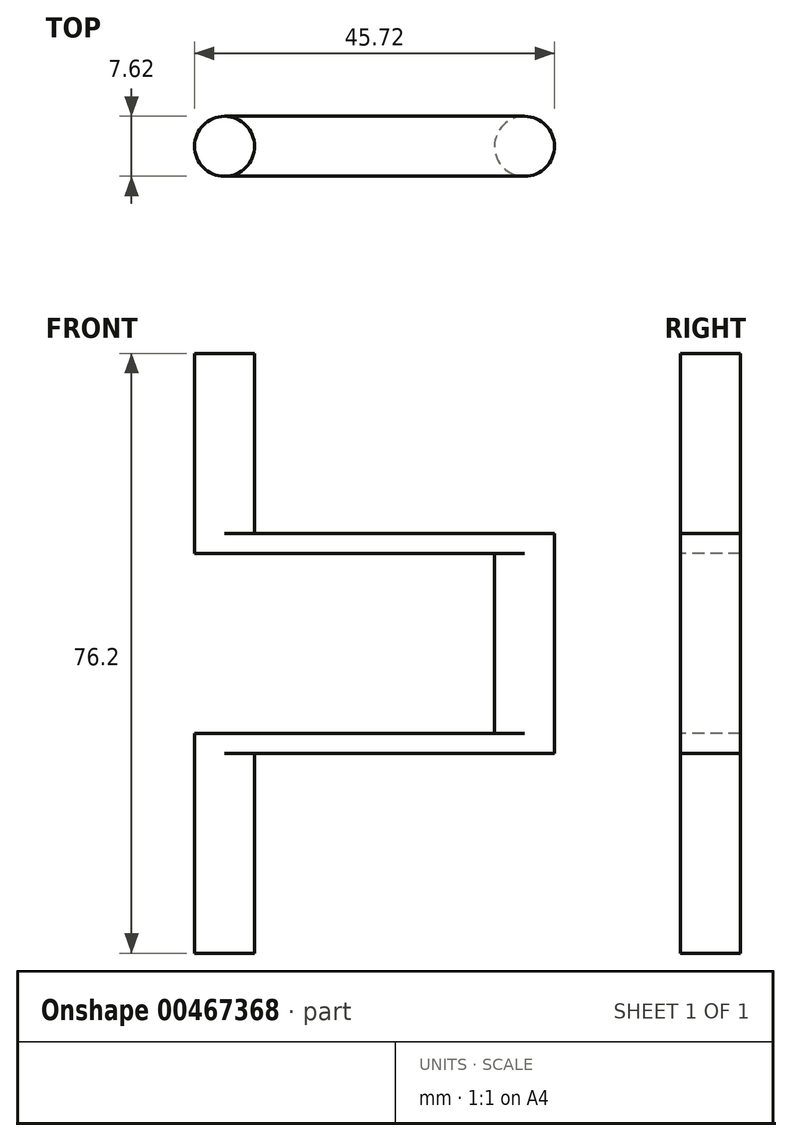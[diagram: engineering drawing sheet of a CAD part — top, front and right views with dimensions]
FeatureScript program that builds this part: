
annotation { "Feature Type Name" : "Feature", "Feature Type Description" : "" }
export const myFeature = defineFeature(function(context is Context, id is Id, definition is map)
    precondition{}
    {
        {
            var Q0;
            Q0=qCreatedBy(makeId("Top.planeOp"),FACE);
            var sketch = newSketch(context, id + "F0", { "sketchPlane" : qUnion([Q0])});
            skLineSegment(sketch, "E0.bottom", {"start": v(19.05, -3.8) * mm, "end": v(-19.05, -3.81) * mm});
            skLineSegment(sketch, "E0.top", {"start": v(19.05, 3.81) * mm, "end": v(-19.05, 3.8) * mm});
            skPoint(sketch, "E0.middle", {"position": v(0, 0) * mm});
            skCircle(sketch, "E1", {"center": v(-19.05, 0) * mm, "radius": 3.81 * mm});
            skCircle(sketch, "E2", {"center": v(19.05, 0) * mm, "radius": 3.81 * mm});
            skSolve(sketch);
        }
        {
            var Q0;
            {var subQ0=sQuery(id+"F0.wireOp",EDGE,"E0.bottom");Q0=makeQuery(id+"F0.imprint","IMPRINT",FACE,{"disambiguationData":[TD([[makeQuery(id+"F0.imprint","IMPRINT",EDGE,{"derivedFrom":subQ0}),-1.0]])]});}
            extrude(context, id + "F1", {"entities" : qUnion([Q0]), "depth" : 2.54 * mm});
        }
        {
            var Q0;
            {var subQ0=sQuery(id+"F0.wireOp",EDGE,"E2");var subQ1=makeQuery(id+"F0.imprint","INTERSECT",VERTEX,{"derivedFrom":[sQuery(id+"F0.wireOp",EDGE,"E0.bottom"),subQ0]});Q0=makeQuery(id+"F0.imprint","IMPRINT",FACE,{"disambiguationData":[TD([[makeQuery(id+"F0.imprint","IMPRINT",EDGE,{"disambiguationData":[TD([[subQ1,1.0]])],"derivedFrom":subQ0}),1.0]])]});}
            extrude(context, id + "F2", {"entities" : qUnion([Q0]), "operationType" : NewBodyOperationType.ADD, "depth" : 25.4 * mm});
        }
        {
            var Q0;
            {var subQ0=sQuery(id+"F0.wireOp",EDGE,"E1");var subQ1=makeQuery(id+"F0.imprint","INTERSECT",VERTEX,{"derivedFrom":[sQuery(id+"F0.wireOp",EDGE,"E0.bottom"),subQ0]});Q0=makeQuery(id+"F0.imprint","IMPRINT",FACE,{"disambiguationData":[TD([[makeQuery(id+"F0.imprint","IMPRINT",EDGE,{"disambiguationData":[TD([[subQ1,1.0]])],"derivedFrom":subQ0}),1.0]])]});}
            extrude(context, id + "F3", {"entities" : qUnion([Q0]), "oppositeDirection" : true, "depth" : 12.7 * mm});
        }
        {
            var Q0;
            {var subQ0=sQuery(id+"F0.wireOp",EDGE,"E1");var subQ1=makeQuery(id+"F0.imprint","INTERSECT",VERTEX,{"derivedFrom":[sQuery(id+"F0.wireOp",EDGE,"E0.bottom"),subQ0]});Q0=makeQuery(id+"F0.imprint","IMPRINT",FACE,{"disambiguationData":[TD([[makeQuery(id+"F0.imprint","IMPRINT",EDGE,{"disambiguationData":[TD([[subQ1,1.0]])],"derivedFrom":subQ0}),1.0]])]});}
            extrude(context, id + "F4", {"entities" : qUnion([Q0]), "depth" : 2.54 * mm});
        }
        {
            var Q0;
            Q0=makeQuery(id+"F2.opExtrude","CAP_FACE",FACE,{"disambiguationData":[OSD([sQuery(id+"F0.wireOp",EDGE,"E2")])],"isStart":false});
            var sketch = newSketch(context, id + "F5", { "sketchPlane" : qUnion([Q0])});
            skLineSegment(sketch, "E3.bottom", {"start": v(19.05, -3.8) * mm, "end": v(-19.05, -3.8) * mm});
            skLineSegment(sketch, "E3.top", {"start": v(19.05, 3.8) * mm, "end": v(-19.05, 3.8) * mm});
            skPoint(sketch, "E3.middle", {"position": v(0, 0) * mm});
            skArc(sketch, "E4", {"start": v(19.05, -3.81) * mm, "mid": v(22.86, 0) * mm, "end": v(19.05, 3.81) * mm});
            skCircle(sketch, "E5", {"center": v(-19.05, 0) * mm, "radius": 3.81 * mm});
            skSolve(sketch);
        }
        {
            var Q0;
            {var subQ0=sQuery(id+"F5.wireOp",EDGE,"E3.bottom");Q0=makeQuery(id+"F5.imprint","IMPRINT",FACE,{"disambiguationData":[TD([[makeQuery(id+"F5.imprint","IMPRINT",EDGE,{"derivedFrom":subQ0}),-1.0]])]});}
            var Q1;
            {var subQ0=sQuery(id+"F5.wireOp",EDGE,"E4");Q1=makeQuery(id+"F5.imprint","IMPRINT",FACE,{"disambiguationData":[TD([[makeQuery(id+"F5.imprint","IMPRINT",EDGE,{"derivedFrom":subQ0}),1.0]])]});}
            extrude(context, id + "F6", {"entities" : qUnion([Q0, Q1]), "operationType" : NewBodyOperationType.ADD, "depth" : 2.54 * mm});
        }
        {
            var Q0;
            {var subQ0=sQuery(id+"F5.wireOp",EDGE,"E5");var subQ1=makeQuery(id+"F5.imprint","INTERSECT",VERTEX,{"derivedFrom":[sQuery(id+"F5.wireOp",EDGE,"E3.bottom"),subQ0]});Q0=makeQuery(id+"F5.imprint","IMPRINT",FACE,{"disambiguationData":[TD([[makeQuery(id+"F5.imprint","IMPRINT",EDGE,{"disambiguationData":[TD([[subQ1,1.0]])],"derivedFrom":subQ0}),1.0]])]});}
            extrude(context, id + "F7", {"entities" : qUnion([Q0]), "operationType" : NewBodyOperationType.ADD, "depth" : 25.4 * mm});
        }
        {
            var Q0;
            Q0=makeQuery(id+"F4.opExtrude","SWEPT_BODY",BODY,{"disambiguationData":[OSD([sQuery(id+"F0.wireOp",EDGE,"E1")])]});
            var Q1;
            Q1=makeQuery(id+"F3.opExtrude","SWEPT_BODY",BODY,{"disambiguationData":[OSD([sQuery(id+"F0.wireOp",EDGE,"E1")])]});
            deleteBodies(context, id + "F8", {"entities" : qUnion([Q0, Q1])});
        }
        {
            var Q0;
            {var subQ0=sQuery(id+"F0.wireOp",EDGE,"E1");var subQ1=makeQuery(id+"F0.imprint","INTERSECT",VERTEX,{"derivedFrom":[sQuery(id+"F0.wireOp",EDGE,"E0.bottom"),subQ0]});Q0=makeQuery(id+"F0.imprint","IMPRINT",FACE,{"disambiguationData":[TD([[makeQuery(id+"F0.imprint","IMPRINT",EDGE,{"disambiguationData":[TD([[subQ1,1.0]])],"derivedFrom":subQ0}),1.0]])]});}
            extrude(context, id + "F9", {"entities" : qUnion([Q0]), "operationType" : NewBodyOperationType.ADD, "depth" : 2.54 * mm});
        }
        {
            var Q0;
            {var subQ0=sQuery(id+"F0.wireOp",EDGE,"E1");var subQ1=makeQuery(id+"F0.imprint","INTERSECT",VERTEX,{"derivedFrom":[sQuery(id+"F0.wireOp",EDGE,"E0.bottom"),subQ0]});Q0=makeQuery(id+"F0.imprint","IMPRINT",FACE,{"disambiguationData":[TD([[makeQuery(id+"F0.imprint","IMPRINT",EDGE,{"disambiguationData":[TD([[subQ1,1.0]])],"derivedFrom":subQ0}),1.0]])]});}
            extrude(context, id + "F10", {"entities" : qUnion([Q0]), "operationType" : NewBodyOperationType.ADD, "oppositeDirection" : true, "depth" : 25.4 * mm});
        }
    });
